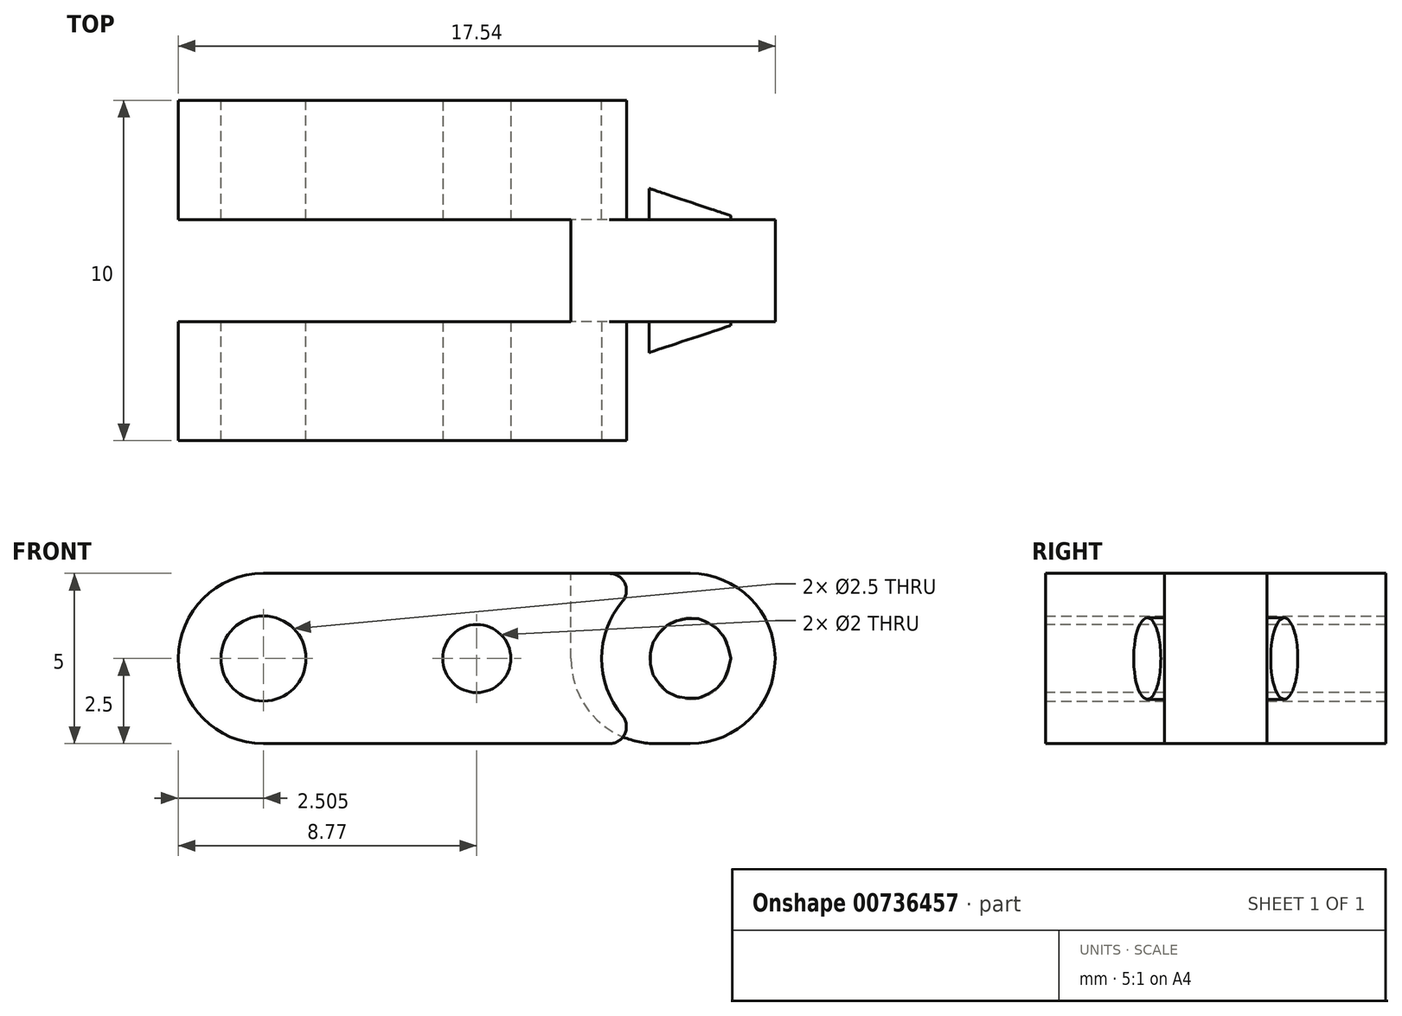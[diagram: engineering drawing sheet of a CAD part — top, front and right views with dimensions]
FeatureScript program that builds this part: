
annotation { "Feature Type Name" : "Feature", "Feature Type Description" : "" }
export const myFeature = defineFeature(function(context is Context, id is Id, definition is map)
    precondition{}
    {
        {
            var Q0;
            Q0=qCreatedBy(makeId("Top.planeOp"),FACE);
            var sketch = newSketch(context, id + "F0", { "sketchPlane" : qUnion([Q0])});
            skLineSegment(sketch, "E0.bottom", {"start": v(8.77, -5) * mm, "end": v(-8.77, -5) * mm});
            skLineSegment(sketch, "E0.top", {"start": v(8.77, 5) * mm, "end": v(-8.77, 5) * mm});
            skLineSegment(sketch, "E0.left", {"start": v(8.77, -5) * mm, "end": v(8.77, 5) * mm});
            skLineSegment(sketch, "E0.right", {"start": v(-8.77, -5) * mm, "end": v(-8.77, 5) * mm});
            skPoint(sketch, "E0.middle", {"position": v(0, 0) * mm});
            skSolve(sketch);
        }
        {
            var Q0;
            Q0 = qSketchRegion(id + "F0", true);
            extrude(context, id + "F1", {"entities" : qUnion([Q0]), "oppositeDirection" : true, "depth" : 5 * mm, "offsetDistance" : 25 * mm});
        }
        {
            var Q0;
            Q0=makeQuery(id+"F1.opExtrude","SWEPT_FACE",FACE,{"disambiguationData":[OSD([sQuery(id+"F0.wireOp",EDGE,"E0.bottom")])]});
            var sketch = newSketch(context, id + "F2", { "sketchPlane" : qUnion([Q0])});
            skArc(sketch, "E1", {"start": v(-6.26, 0) * mm, "mid": v(-8.77, -2.5) * mm, "end": v(-6.26, -5) * mm});
            skArc(sketch, "E2", {"start": v(6.26, -5) * mm, "mid": v(8.77, -2.5) * mm, "end": v(6.26, 0) * mm});
            skSolve(sketch);
        }
        {
            var Q0;
            {var subQ0=sQuery(id+"F2.wireOp",EDGE,"E2");var subQ1=sQuery(id+"F0.wireOp",EDGE,"E0.bottom");var subQ2=makeQuery(id+"F1.opExtrude","CAP_EDGE",EDGE,{"disambiguationData":[OSD([subQ1])],"isStart":true});var subQ3=makeQuery(id+"F2.imprint","INTERSECT",VERTEX,{"derivedFrom":[subQ2,subQ0]});Q0=makeQuery(id+"F2.imprint","IMPRINT",FACE,{"disambiguationData":[TD([[makeQuery(id+"F2.imprint","IMPRINT",EDGE,{"disambiguationData":[TD([[subQ3,1.0]])],"derivedFrom":subQ0}),-1.0]])]});}
            var Q1;
            {var subQ0=sQuery(id+"F2.wireOp",EDGE,"E2");var subQ1=sQuery(id+"F0.wireOp",EDGE,"E0.bottom");var subQ2=makeQuery(id+"F1.opExtrude","CAP_EDGE",EDGE,{"disambiguationData":[OSD([subQ1])],"isStart":false});var subQ3=makeQuery(id+"F2.imprint","INTERSECT",VERTEX,{"derivedFrom":[subQ2,subQ0]});Q1=makeQuery(id+"F2.imprint","IMPRINT",FACE,{"disambiguationData":[TD([[makeQuery(id+"F2.imprint","IMPRINT",EDGE,{"disambiguationData":[TD([[subQ3,-1.0]])],"derivedFrom":subQ0}),-1.0]])]});}
            var Q2;
            {var subQ0=sQuery(id+"F2.wireOp",EDGE,"E1");var subQ1=sQuery(id+"F0.wireOp",EDGE,"E0.bottom");var subQ2=makeQuery(id+"F1.opExtrude","CAP_EDGE",EDGE,{"disambiguationData":[OSD([subQ1])],"isStart":false});var subQ3=makeQuery(id+"F2.imprint","INTERSECT",VERTEX,{"derivedFrom":[subQ2,subQ0]});Q2=makeQuery(id+"F2.imprint","IMPRINT",FACE,{"disambiguationData":[TD([[makeQuery(id+"F2.imprint","IMPRINT",EDGE,{"disambiguationData":[TD([[subQ3,1.0]])],"derivedFrom":subQ0}),-1.0]])]});}
            var Q3;
            {var subQ0=sQuery(id+"F2.wireOp",EDGE,"E1");var subQ1=sQuery(id+"F0.wireOp",EDGE,"E0.bottom");var subQ2=makeQuery(id+"F1.opExtrude","CAP_EDGE",EDGE,{"disambiguationData":[OSD([subQ1])],"isStart":true});var subQ3=makeQuery(id+"F2.imprint","INTERSECT",VERTEX,{"derivedFrom":[subQ2,subQ0]});Q3=makeQuery(id+"F2.imprint","IMPRINT",FACE,{"disambiguationData":[TD([[makeQuery(id+"F2.imprint","IMPRINT",EDGE,{"disambiguationData":[TD([[subQ3,-1.0]])],"derivedFrom":subQ0}),-1.0]])]});}
            extrude(context, id + "F3", {"entities" : qUnion([Q0, Q1, Q2, Q3]), "operationType" : NewBodyOperationType.REMOVE, "endBound" : BoundingType.THROUGH_ALL, "oppositeDirection" : true, "depth" : 25 * mm, "offsetDistance" : 25 * mm});
        }
        {
            var Q0;
            Q0=makeQuery(id+"F1.opExtrude","SWEPT_FACE",FACE,{"disambiguationData":[OSD([sQuery(id+"F0.wireOp",EDGE,"E0.top")])]});
            var sketch = newSketch(context, id + "F4", { "sketchPlane" : qUnion([Q0])});
            skCircle(sketch, "E3", {"center": v(6.26, -2.5) * mm, "radius": 1.25 * mm});
            skSolve(sketch);
        }
        {
            var Q0;
            Q0 = qSketchRegion(id + "F4", true);
            extrude(context, id + "F5", {"entities" : qUnion([Q0]), "operationType" : NewBodyOperationType.REMOVE, "endBound" : BoundingType.THROUGH_ALL, "oppositeDirection" : true, "depth" : 25 * mm, "offsetDistance" : 25 * mm});
        }
        {
            var Q0;
            Q0=makeQuery(id+"F1.opExtrude","SWEPT_FACE",FACE,{"disambiguationData":[OSD([sQuery(id+"F0.wireOp",EDGE,"E0.top")])]});
            var sketch = newSketch(context, id + "F6", { "sketchPlane" : qUnion([Q0])});
            skCircle(sketch, "E4", {"center": v(-6.26, -2.5) * mm, "radius": 2.6 * mm});
            skSolve(sketch);
        }
        {
            var Q0;
            Q0 = qSketchRegion(id + "F6", true);
            extrude(context, id + "F7", {"entities" : qUnion([Q0]), "operationType" : NewBodyOperationType.REMOVE, "oppositeDirection" : true, "depth" : 3.5 * mm, "offsetDistance" : 25 * mm});
        }
        {
            var Q0;
            Q0=makeQuery(id+"F1.opExtrude","SWEPT_FACE",FACE,{"disambiguationData":[OSD([sQuery(id+"F0.wireOp",EDGE,"E0.bottom")])]});
            var sketch = newSketch(context, id + "F8", { "sketchPlane" : qUnion([Q0])});
            skCircle(sketch, "E5", {"center": v(6.26, -2.5) * mm, "radius": 2.6 * mm});
            skSolve(sketch);
        }
        {
            var Q0;
            Q0 = qSketchRegion(id + "F8", true);
            extrude(context, id + "F9", {"entities" : qUnion([Q0]), "operationType" : NewBodyOperationType.REMOVE, "oppositeDirection" : true, "depth" : 3.5 * mm, "offsetDistance" : 25 * mm});
        }
        {
            var Q0;
            Q0=makeQuery(id+"F1.opExtrude","CAP_FACE",FACE,{"disambiguationData":[OSD([sQuery(id+"F0.wireOp",EDGE,"E0.bottom"),sQuery(id+"F0.wireOp",EDGE,"E0.top"),sQuery(id+"F0.wireOp",EDGE,"E0.left"),sQuery(id+"F0.wireOp",EDGE,"E0.right")])],"isStart":true});
            var sketch = newSketch(context, id + "F10", { "sketchPlane" : qUnion([Q0])});
            skPoint(sketch, "E6.middle", {"position": v(0, 0) * mm});
            skLineSegment(sketch, "E7.bottom", {"start": v(2.76, 1.5) * mm, "end": v(-11.27, 1.5) * mm});
            skLineSegment(sketch, "E7.top", {"start": v(2.77, -1.5) * mm, "end": v(-11.26, -1.5) * mm});
            skLineSegment(sketch, "E7.left", {"start": v(2.76, 1.5) * mm, "end": v(2.77, -1.5) * mm});
            skLineSegment(sketch, "E7.right", {"start": v(-11.27, 1.5) * mm, "end": v(-11.26, -1.5) * mm});
            skSolve(sketch);
        }
        {
            var Q0;
            Q0 = qSketchRegion(id + "F10", true);
            extrude(context, id + "F11", {"entities" : qUnion([Q0]), "operationType" : NewBodyOperationType.REMOVE, "endBound" : BoundingType.THROUGH_ALL, "oppositeDirection" : true, "depth" : 25 * mm, "offsetDistance" : 25 * mm});
        }
        {
            var Q0;
            Q0=makeQuery(id+"F1.opExtrude","SWEPT_FACE",FACE,{"disambiguationData":[OSD([sQuery(id+"F0.wireOp",EDGE,"E0.top")])]});
            var sketch = newSketch(context, id + "F12", { "sketchPlane" : qUnion([Q0])});
            skCircle(sketch, "E8", {"center": v(-6.26, -2.5) * mm, "radius": 1.2 * mm});
            skSolve(sketch);
        }
        {
            var Q0;
            Q0 = qSketchRegion(id + "F12", true);
            extrude(context, id + "F13", {"entities" : qUnion([Q0]), "operationType" : NewBodyOperationType.ADD, "oppositeDirection" : true, "depth" : 10 * mm, "offsetDistance" : 25 * mm});
        }
        {
            var Q0;
            Q0=makeQuery(id+"F7.boolean.opBoolean","INTERSECT",EDGE,{"derivedFrom":[makeQuery(id+"F1.opExtrude","CAP_FACE",FACE,{"disambiguationData":[OSD([sQuery(id+"F0.wireOp",EDGE,"E0.bottom"),sQuery(id+"F0.wireOp",EDGE,"E0.top"),sQuery(id+"F0.wireOp",EDGE,"E0.left"),sQuery(id+"F0.wireOp",EDGE,"E0.right")])],"isStart":true}),makeQuery(id+"F7.opExtrude","SWEPT_FACE",FACE,{"disambiguationData":[OSD([sQuery(id+"F6.wireOp",EDGE,"E4")])]})]});
            var Q1;
            Q1=makeQuery(id+"F9.boolean.opBoolean","INTERSECT",EDGE,{"derivedFrom":[makeQuery(id+"F1.opExtrude","CAP_FACE",FACE,{"disambiguationData":[OSD([sQuery(id+"F0.wireOp",EDGE,"E0.bottom"),sQuery(id+"F0.wireOp",EDGE,"E0.top"),sQuery(id+"F0.wireOp",EDGE,"E0.left"),sQuery(id+"F0.wireOp",EDGE,"E0.right")])],"isStart":true}),makeQuery(id+"F9.opExtrude","SWEPT_FACE",FACE,{"disambiguationData":[OSD([sQuery(id+"F8.wireOp",EDGE,"E5")])]})]});
            var Q2;
            Q2=makeQuery(id+"F9.boolean.opBoolean","INTERSECT",EDGE,{"derivedFrom":[makeQuery(id+"F1.opExtrude","CAP_FACE",FACE,{"disambiguationData":[OSD([sQuery(id+"F0.wireOp",EDGE,"E0.bottom"),sQuery(id+"F0.wireOp",EDGE,"E0.top"),sQuery(id+"F0.wireOp",EDGE,"E0.left"),sQuery(id+"F0.wireOp",EDGE,"E0.right")])],"isStart":false}),makeQuery(id+"F9.opExtrude","SWEPT_FACE",FACE,{"disambiguationData":[OSD([sQuery(id+"F8.wireOp",EDGE,"E5")])]})]});
            var Q3;
            Q3=makeQuery(id+"F7.boolean.opBoolean","INTERSECT",EDGE,{"derivedFrom":[makeQuery(id+"F1.opExtrude","CAP_FACE",FACE,{"disambiguationData":[OSD([sQuery(id+"F0.wireOp",EDGE,"E0.bottom"),sQuery(id+"F0.wireOp",EDGE,"E0.top"),sQuery(id+"F0.wireOp",EDGE,"E0.left"),sQuery(id+"F0.wireOp",EDGE,"E0.right")])],"isStart":false}),makeQuery(id+"F7.opExtrude","SWEPT_FACE",FACE,{"disambiguationData":[OSD([sQuery(id+"F6.wireOp",EDGE,"E4")])]})]});
            fillet(context, id + "F14", {"entities" : qUnion([Q0, Q1, Q2, Q3]), "radius" : .5 * mm, "tangentPropagation" : true, "allowEdgeOverflow" : false});
        }
        {
            var Q0;
            Q0=makeQuery(id+"F1.opExtrude","CAP_FACE",FACE,{"disambiguationData":[OSD([sQuery(id+"F0.wireOp",EDGE,"E0.bottom"),sQuery(id+"F0.wireOp",EDGE,"E0.top"),sQuery(id+"F0.wireOp",EDGE,"E0.left"),sQuery(id+"F0.wireOp",EDGE,"E0.right")])],"isStart":false});
            var sketch = newSketch(context, id + "F15", { "sketchPlane" : qUnion([Q0])});
            skLineSegment(sketch, "E9", {"start": v(8, 5.5) * mm, "end": v(8, 2.48) * mm});
            skLineSegment(sketch, "E10", {"start": v(8, 2.48) * mm, "end": v(7.8, 1.5) * mm});
            skLineSegment(sketch, "E11", {"start": v(8, -5.5) * mm, "end": v(8, -2.48) * mm});
            skLineSegment(sketch, "E12", {"start": v(8, -2.48) * mm, "end": v(7.8, -1.5) * mm});
            skLineSegment(sketch, "E13", {"start": v(7.8, -1.5) * mm, "end": v(4.8, -2.5) * mm});
            skLineSegment(sketch, "E14", {"start": v(4.8, -2.5) * mm, "end": v(4.8, -5.5) * mm});
            skLineSegment(sketch, "E15", {"start": v(4.8, -5.5) * mm, "end": v(8, -5.5) * mm});
            skLineSegment(sketch, "E16", {"start": v(8, 5.5) * mm, "end": v(4.8, 5.5) * mm});
            skLineSegment(sketch, "E17", {"start": v(4.8, 5.5) * mm, "end": v(4.8, 2.5) * mm});
            skLineSegment(sketch, "E18", {"start": v(4.8, 2.5) * mm, "end": v(7.8, 1.5) * mm});
            skSolve(sketch);
        }
        {
            var Q0;
            Q0 = qSketchRegion(id + "F15", true);
            extrude(context, id + "F16", {"entities" : qUnion([Q0]), "operationType" : NewBodyOperationType.REMOVE, "endBound" : BoundingType.THROUGH_ALL, "oppositeDirection" : true, "depth" : 25 * mm, "offsetDistance" : 25 * mm});
        }
        {
            var Q0;
            Q0=makeQuery(id+"F11.boolean.opBoolean","COPY",EDGE,{"derivedFrom":makeQuery(id+"F11.opExtrude","CAP_EDGE",EDGE,{"disambiguationData":[OSD([sQuery(id+"F10.wireOp",EDGE,"E7.left")])],"isStart":true})});
            var Q1;
            Q1=makeQuery(id+"F11.boolean.opBoolean","INTERSECT",EDGE,{"derivedFrom":[makeQuery(id+"F1.opExtrude","CAP_FACE",FACE,{"disambiguationData":[OSD([sQuery(id+"F0.wireOp",EDGE,"E0.bottom"),sQuery(id+"F0.wireOp",EDGE,"E0.top"),sQuery(id+"F0.wireOp",EDGE,"E0.left"),sQuery(id+"F0.wireOp",EDGE,"E0.right")])],"isStart":false}),makeQuery(id+"F11.opExtrude","SWEPT_FACE",FACE,{"disambiguationData":[OSD([sQuery(id+"F10.wireOp",EDGE,"E7.left")])]})]});
            fillet(context, id + "F17", {"entities" : qUnion([Q0, Q1]), "radius" : 2.5 * mm, "tangentPropagation" : true, "allowEdgeOverflow" : false});
        }
        {
            var Q0;
            Q0=makeQuery(id+"F1.opExtrude","SWEPT_FACE",FACE,{"disambiguationData":[OSD([sQuery(id+"F0.wireOp",EDGE,"E0.bottom")])]});
            var sketch = newSketch(context, id + "F18", { "sketchPlane" : qUnion([Q0])});
            skLineSegment(sketch, "E19", {"start": v(-6.26, -2.5) * mm, "end": v(6.27, -2.5) * mm, "construction": true});
            skCircle(sketch, "E20", {"center": v(0, -2.5) * mm, "radius": 1 * mm});
            skSolve(sketch);
        }
        {
            var Q0;
            Q0 = qSketchRegion(id + "F18", true);
            extrude(context, id + "F19", {"entities" : qUnion([Q0]), "operationType" : NewBodyOperationType.REMOVE, "endBound" : BoundingType.THROUGH_ALL, "oppositeDirection" : true, "depth" : 25 * mm, "offsetDistance" : 25 * mm});
        }
    });
